# Revit family: Hager-Univers-IP44-D161-Cl.II-FWB-encl--PL-pl
name_source: partatom
category: Equipement électrique
units: mm (PartAtom-declared; Revit-internal decimal feet)

## family parameters
Configuration du panneau = Deux colonnes, circuits au sein
Cote de connecteur circulaire = Utiliser le diamètre
Couper avec des vides une fois chargée = Non
Hôte = Face
Partagée = Non
Point de calcul de pièce = Non
Type d'élément = Tableau de raccordement

## types (19) — shared parameters
Commentaires du type = Univers
EF000003 - Sposób montażu = EV000384 - Montaż natynkowy
EF000007 - Kolor = EV000202 - Biały
EF000049 - Głębokość = 161 mm  [stored 0.528215 ft]
EF000116 - Numer RAL = 9010
EF000118 - Z płytą montażową = Non
EF001088 - Możliwość rozbudowy = Oui
EF001596 - Materiał obudowy = EV000179 - Stal
EF001613 - Podtrzymanie funkcji = EV000494 - Brak
EF002950 - Szerokość wyrażona liczbą modułów = 12
EF003532 - Do zastosowań zewnętrznych = Non
EF004293 - Odporność udarowa = EV006815 - IK09
EF005474 - Stopień ochrony (IP) = EV006418 - IP44
EF006244 - Transparentna pokrywa/drzwi = Non
EF006306 - Z zamkiem = Non
EF007800 - Do ochrony odgromowej = Non
EF008873 - Prąd znamionowy (In) = 125 A
EF015940 - Pokrywa z wyzwalaczem nadciśnieniowym = Non
Fabricant = Hager
HG000002 - Z drzwiami lub pokrywą = Oui
HG000003 - Zakres = Univers
HG000006 - Montaż podtynkowy = Non
HG000023 - Obudowa dwusekcyjna = Non
HG000024 - Wysokość części dolnej = 800 mm  [stored 2.62467 ft]
HG000026 - Stojąca = Non
zero-valued in all types: EF000218 - Głębokość wbudowania, EF000266 - Liczba rzędów, Elévation par défaut, HG000027 - Wysokość cokołu

## per-type parameters (varying)
| type | EF000008 - Szerokość | EF000040 - Wysokość | EF000339 - Rodzaj pokrywy | EF000437 - Liczba wejść kablowych | EF001131 - Głębokość wewnętrzna | EF004427 - Liczba modułów | EF004464 - Rodzaj drzwi | EF009170 - Obudowa z materiału o wysokiej wytrzymałości mechanicznej | EF009171 - Drzwi/pokrywa z materiału o wysokiej wytrzymałości mechanicznej | EF009212 - Wykonanie pokrywy | EF009554 - Liczba otworów pod flansze | HG000004 - Referencja producenta | HG000009 - Drzwi dwuskrzydłowe | HG000010 - Drzwi asymetryczne |
| Montaż natynkowy IP44 S1050 W1100 G161  - FWB74D | 1050 mm | 1100 mm | EV000494 - Brak | 16 | 160 mm  [stored 0.524934 ft] | 336 | EV000494 - Brak | 1 mm  [stored 0.00328084 ft] | 1 mm  [stored 0.00328084 ft] | EV000116 - Zamknięty | 8 | FWB74D | Oui | Non |
| Montaż natynkowy IP44 S1050 W500 G161  - FWB34D | 1050 mm | 500 mm  [stored 1.64042 ft] | EV004216 - Drzwi | 16 | 156 mm  [stored 0.511811 ft] | 144 | EV003602 - Podwójny | 1 mm  [stored 0.00328084 ft] | 1 mm  [stored 0.00328084 ft] | EV000116 - Zamknięty | 8 | FWB34D | Oui | Non |
| Montaż natynkowy IP44 S1050 W650 G161  - FWB44D | 1050 mm | 650 mm  [stored 2.13255 ft] | EV004216 - Drzwi | 16 | 156 mm  [stored 0.511811 ft] | 192 | EV003602 - Podwójny | 1 mm  [stored 0.00328084 ft] | 1 mm  [stored 0.00328084 ft] | EV000116 - Zamknięty | 8 | FWB44D | Oui | Non |
| Montaż natynkowy IP44 S1050 W800 G161  - FWB54D | 1050 mm | 800 mm  [stored 2.62467 ft] | EV004216 - Drzwi | 16 | 156 mm  [stored 0.511811 ft] | 240 | EV002646 - Pojedynczy | 1 mm  [stored 0.00328084 ft] | 1 mm  [stored 0.00328084 ft] | EV000116 - Zamknięty | 8 | FWB54D | Oui | Non |
| Montaż natynkowy IP44 S1050 W950 G161  - FWB64D | 1050 mm | 950 mm  [stored 3.1168 ft] | EV004216 - Drzwi | 16 | 156 mm  [stored 0.511811 ft] | 288 | EV003602 - Podwójny | 1 mm  [stored 0.00328084 ft] | 1 mm  [stored 0.00328084 ft] | EV000116 - Zamknięty | 8 | FWB64D | Oui | Non |
| Montaż natynkowy IP44 S300 W1100 G161  - FWB71D | 300 mm | 1100 mm | EV004216 - Drzwi | 4 | 160 mm  [stored 0.524934 ft] | 84 | EV000494 - Brak | 1 mm  [stored 0.00328084 ft] | 1 mm  [stored 0.00328084 ft] | EV000116 - Zamknięty | 2 | FWB71D | Non | Non |
| Montaż natynkowy IP44 S300 W650 G161  - FWB41D | 300 mm | 650 mm  [stored 2.13255 ft] | EV004216 - Drzwi | 4 | 160 mm  [stored 0.524934 ft] | 48 | EV000494 - Brak | 2 mm  [stored 0.00656168 ft] | 2 mm  [stored 0.00656168 ft] | EV000116 - Zamknięty | 2 | FWB41D | Non | Non |
| Montaż natynkowy IP44 S300 W800 G161  - FWB51D | 300 mm | 800 mm  [stored 2.62467 ft] | EV004216 - Drzwi | 4 | 160 mm  [stored 0.524934 ft] | 60 | EV000494 - Brak | 1 mm  [stored 0.00328084 ft] | 1 mm  [stored 0.00328084 ft] | EV000116 - Zamknięty | 2 | FWB51D | Non | Non |
| Montaż natynkowy IP44 S300 W950 G161  - FWB61D | 300 mm | 950 mm  [stored 3.1168 ft] | EV004216 - Drzwi | 4 | 160 mm  [stored 0.524934 ft] | 72 | EV000494 - Brak | 1 mm  [stored 0.00328084 ft] | 1 mm  [stored 0.00328084 ft] | EV000116 - Zamknięty | 2 | FWB61D | Non | Non |
| Montaż natynkowy IP44 S550 W1100 G161  - FWB72D | 550 mm | 1100 mm | EV004216 - Drzwi | 8 | 160 mm  [stored 0.524934 ft] | 168 | EV000494 - Brak | 1 mm  [stored 0.00328084 ft] | 1 mm  [stored 0.00328084 ft] | EV000116 - Zamknięty | 4 | FWB72D | Non | Non |
| Montaż natynkowy IP44 S550 W500 G161  - FWB32D | 550 mm | 500 mm  [stored 1.64042 ft] | EV000494 - Brak | 8 | 156 mm  [stored 0.511811 ft] | 72 | EV002646 - Pojedynczy | 2 mm  [stored 0.00656168 ft] | 2 mm  [stored 0.00656168 ft] | EV000116 - Zamknięty | 4 | FWB32D | Non | Non |
| Montaż natynkowy IP44 S550 W650 G161  - FWB42D | 550 mm | 650 mm  [stored 2.13255 ft] | EV004216 - Drzwi | 8 | 160 mm  [stored 0.524934 ft] | 96 | EV000494 - Brak | 1 mm  [stored 0.00328084 ft] | 1 mm  [stored 0.00328084 ft] | EV000116 - Zamknięty | 4 | FWB42D | Non | Non |
| Montaż natynkowy IP44 S550 W800 G161  - FWB52D | 550 mm | 800 mm  [stored 2.62467 ft] | EV004216 - Drzwi | 8 | 160 mm  [stored 0.524934 ft] | 120 | EV000494 - Brak | 1 mm  [stored 0.00328084 ft] | 1 mm  [stored 0.00328084 ft] | EV000116 - Zamknięty | 4 | FWB52D | Non | Non |
| Montaż natynkowy IP44 S550 W950 G161  - FWB62D | 550 mm | 950 mm  [stored 3.1168 ft] | EV004216 - Drzwi | 8 | 160 mm  [stored 0.524934 ft] | 144 | EV000494 - Brak | 1 mm  [stored 0.00328084 ft] | 1 mm  [stored 0.00328084 ft] | EV000116 - Zamknięty | 4 | FWB62D | Non | Non |
| Montaż natynkowy IP44 S800 W1100 G161  - FWB73D | 800 mm  [stored 2.62467 ft] | 1100 mm | EV004216 - Drzwi | 12 | 156 mm  [stored 0.511811 ft] | 252 | EV003602 - Podwójny | 1 mm  [stored 0.00328084 ft] | 1 mm  [stored 0.00328084 ft] | EV000116 - Zamknięty | 6 | FWB73D | Oui | Oui |
| Montaż natynkowy IP44 S800 W500 G161  - FWB33D | 800 mm  [stored 2.62467 ft] | 500 mm  [stored 1.64042 ft] | EV004216 - Drzwi | 12 | 160 mm  [stored 0.524934 ft] | 108 | EV000494 - Brak | 1 mm  [stored 0.00328084 ft] | 1 mm  [stored 0.00328084 ft] | EV000116 - Zamknięty | 6 | FWB33D | Oui | Oui |
| Montaż natynkowy IP44 S800 W650 G161  - FWB43D | 800 mm  [stored 2.62467 ft] | 650 mm  [stored 2.13255 ft] | EV004216 - Drzwi | 12 | 160 mm  [stored 0.524934 ft] | 144 | EV000494 - Brak | 2 mm  [stored 0.00656168 ft] | 1 mm  [stored 0.00328084 ft] | EV009916 - Z otworem | 6 | FWB43D | Oui | Oui |
| Montaż natynkowy IP44 S800 W800 G161  - FWB53D | 800 mm  [stored 2.62467 ft] | 800 mm  [stored 2.62467 ft] | EV004216 - Drzwi | 12 | 160 mm  [stored 0.524934 ft] | 180 | EV000494 - Brak | 2 mm  [stored 0.00656168 ft] | 1 mm  [stored 0.00328084 ft] | EV000116 - Zamknięty | 6 | FWB53D | Oui | Oui |
| Montaż natynkowy IP44 S800 W950 G161  - FWB63D | 800 mm  [stored 2.62467 ft] | 950 mm  [stored 3.1168 ft] | EV004216 - Drzwi | 12 | 156 mm  [stored 0.511811 ft] | 216 | EV000494 - Brak | 1 mm  [stored 0.00328084 ft] | 1 mm  [stored 0.00328084 ft] | EV000116 - Zamknięty | 6 | FWB63D | Oui | Oui |

note: [stored X ft] marks values corroborated as IEEE doubles in the binary element streams (Revit-internal decimal feet)

## geometry (parser evidence)
native form markers: Sweep x10
no freeform markers — native parametric forms only
